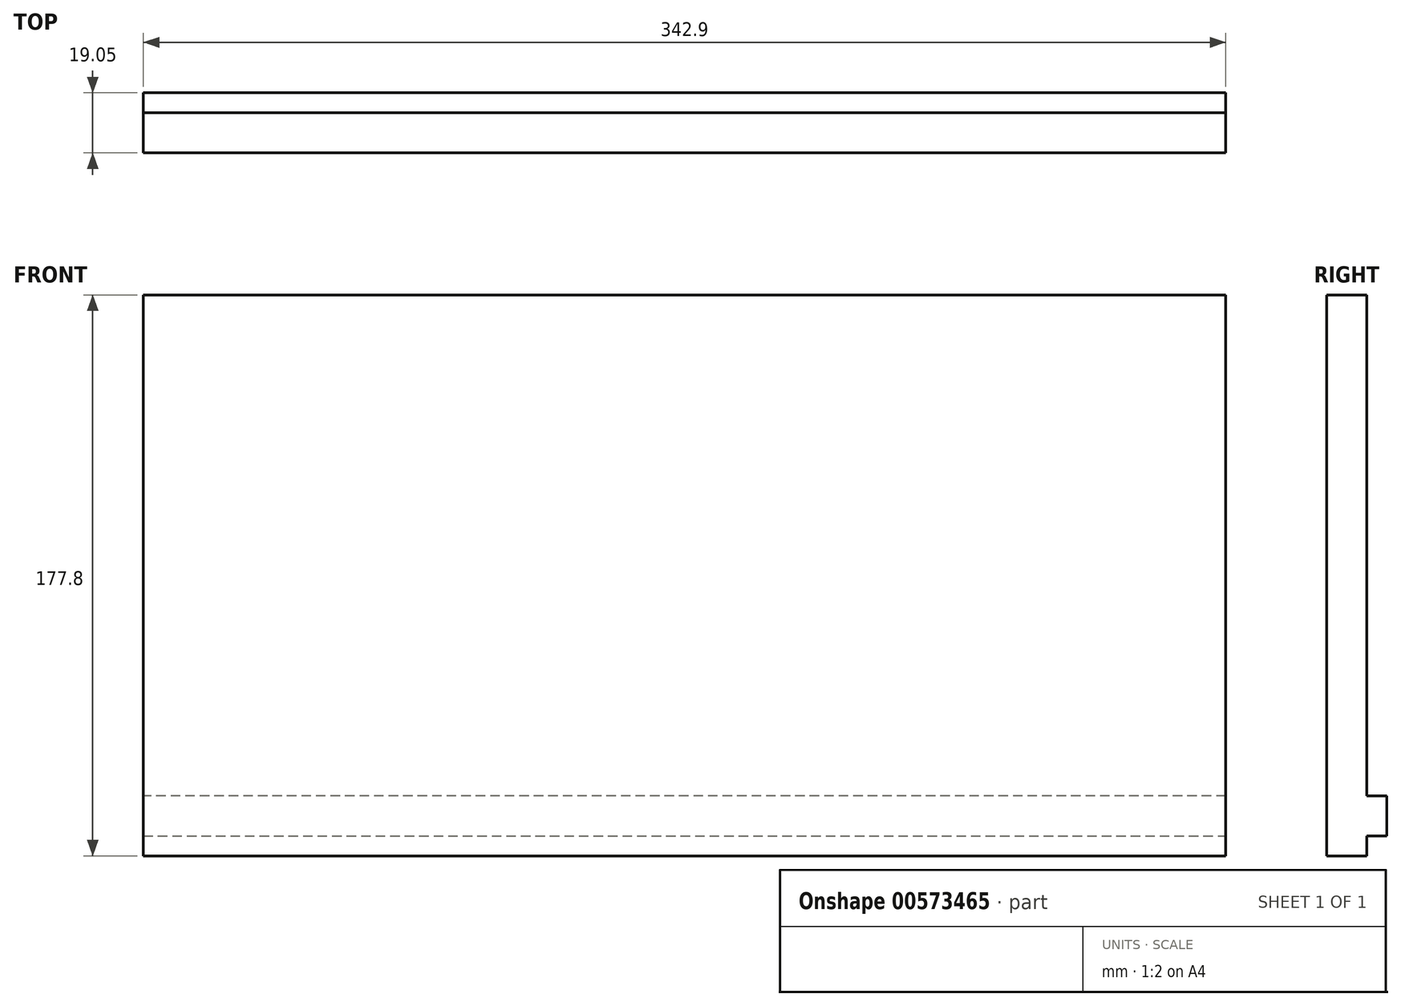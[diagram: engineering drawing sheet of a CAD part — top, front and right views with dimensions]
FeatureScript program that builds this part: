
annotation { "Feature Type Name" : "Feature", "Feature Type Description" : "" }
export const myFeature = defineFeature(function(context is Context, id is Id, definition is map)
    precondition{}
    {
        {
            var Q0;
            Q0=qCreatedBy(makeId("Front.planeOp"),FACE);
            var sketch = newSketch(context, id + "F0", { "sketchPlane" : qUnion([Q0])});
            skLineSegment(sketch, "E0.bottom", {"start": v(-171.45, 88.9) * mm, "end": v(171.45, 88.9) * mm});
            skLineSegment(sketch, "E0.top", {"start": v(-171.45, -88.9) * mm, "end": v(171.45, -88.9) * mm});
            skLineSegment(sketch, "E0.left", {"start": v(-171.45, 88.9) * mm, "end": v(-171.45, -88.9) * mm});
            skLineSegment(sketch, "E0.right", {"start": v(171.45, 88.9) * mm, "end": v(171.45, -88.9) * mm});
            skPoint(sketch, "E0.middle", {"position": v(0, 0) * mm});
            skSolve(sketch);
        }
        {
            var Q0;
            Q0=makeQuery(id+"F0.imprint","IMPRINT",FACE,{"disambiguationData":[TD([[makeQuery(id+"F0.imprint","IMPRINT",EDGE,{"derivedFrom":sQuery(id+"F0.wireOp",EDGE,"E0.bottom")}),-1.0]])]});
            extrude(context, id + "F1", {"entities" : qUnion([Q0]), "depth" : 12.7 * mm, "offsetDistance" : 25.4 * mm});
        }
        {
            var Q0;
            Q0=makeQuery(id+"F1.opExtrude","CAP_FACE",FACE,{"disambiguationData":[OSD([sQuery(id+"F0.wireOp",EDGE,"E0.bottom"),sQuery(id+"F0.wireOp",EDGE,"E0.top"),sQuery(id+"F0.wireOp",EDGE,"E0.left"),sQuery(id+"F0.wireOp",EDGE,"E0.right")])],"isStart":true});
            var sketch = newSketch(context, id + "F2", { "sketchPlane" : qUnion([Q0])});
            skLineSegment(sketch, "E1", {"start": v(-171.45, -88.9) * mm, "end": v(-171.45, -82.55) * mm});
            skLineSegment(sketch, "E2", {"start": v(-171.45, -82.55) * mm, "end": v(-171.45, -69.85) * mm});
            skLineSegment(sketch, "E3", {"start": v(-171.45, -69.85) * mm, "end": v(171.45, -69.85) * mm});
            skLineSegment(sketch, "E4", {"start": v(171.45, -69.85) * mm, "end": v(171.45, -82.55) * mm});
            skLineSegment(sketch, "E5", {"start": v(171.45, -82.55) * mm, "end": v(-171.45, -82.55) * mm});
            skSolve(sketch);
        }
        {
            var Q0;
            Q0=makeQuery(id+"F2.imprint","IMPRINT",FACE,{"disambiguationData":[TD([[makeQuery(id+"F2.imprint","IMPRINT",EDGE,{"derivedFrom":sQuery(id+"F2.wireOp",EDGE,"E2")}),1.0]])]});
            extrude(context, id + "F3", {"entities" : qUnion([Q0]), "operationType" : NewBodyOperationType.ADD, "depth" : 6.35 * mm, "offsetDistance" : 25.4 * mm});
        }
    });
